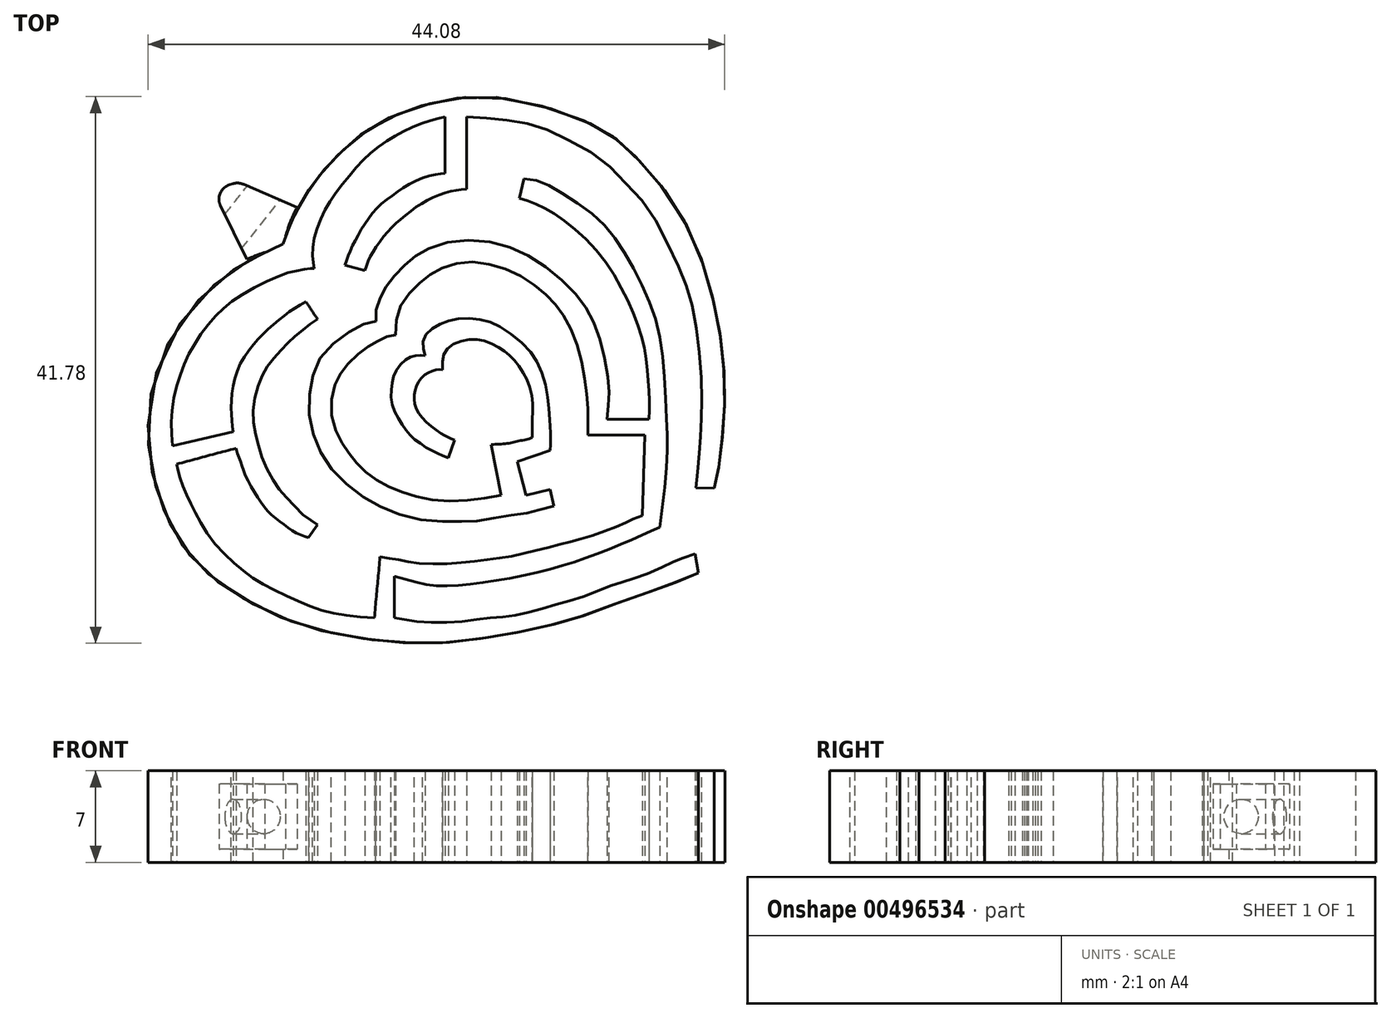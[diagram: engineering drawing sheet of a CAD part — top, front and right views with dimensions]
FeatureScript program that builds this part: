
annotation { "Feature Type Name" : "Feature", "Feature Type Description" : "" }
export const myFeature = defineFeature(function(context is Context, id is Id, definition is map)
    precondition{}
    {
        {
            var Q0;
            Q0=qCreatedBy(makeId("Top.planeOp"),FACE);
            var sketch = newSketch(context, id + "F0", { "sketchPlane" : qUnion([Q0])});
            skFitSpline(sketch, "E0", {"points": [v(62.05, 22.52) * mm, v(60.63, 22.56) * mm], "startDerivative": vector(-1.42, 0.04) * mm, "endDerivative": vector(-1.42, 0.04) * mm});
            skFitSpline(sketch, "E1", {"points": [v(60.63, 22.56) * mm, v(60.77, 23.68) * mm, v(60.9, 25.24) * mm, v(60.98, 26.5) * mm, v(61.06, 28.05) * mm, v(61.1, 29.64) * mm, v(60.96, 32.3) * mm, v(60.63, 35.06) * mm, v(60.14, 37.28) * mm, v(59.52, 38.95) * mm, v(58.29, 41.63) * mm, v(56.87, 44.04) * mm, v(55.17, 45.95) * mm, v(53.45, 47.62) * mm, v(50.93, 49.09) * mm, v(48.74, 50.12) * mm, v(46.91, 50.53) * mm, v(44.93, 50.79) * mm, v(43.1, 50.9) * mm], "startDerivative": vector(3.34, 25.94) * mm, "endDerivative": vector(-34.59, 1.48) * mm});
            skFitSpline(sketch, "E2", {"points": [v(43.1, 50.9) * mm, v(43.1, 45.38) * mm], "startDerivative": vector(0, -5.52) * mm, "endDerivative": vector(0, -5.52) * mm});
            skFitSpline(sketch, "E3", {"points": [v(43.1, 45.38) * mm, v(42.1, 45.24) * mm, v(40.77, 44.82) * mm, v(39.39, 44.09) * mm, v(38.14, 43.1) * mm, v(37.13, 42.18) * mm, v(36.24, 41.01) * mm, v(35.66, 40.02) * mm, v(35.32, 39.16) * mm], "startDerivative": vector(-9.38, -0.74) * mm, "endDerivative": vector(-3.58, -8.09) * mm});
            skFitSpline(sketch, "E4", {"points": [v(35.32, 39.16) * mm, v(33.83, 39.57) * mm], "startDerivative": vector(-1.5, 0.4) * mm, "endDerivative": vector(-1.5, 0.4) * mm});
            skFitSpline(sketch, "E5", {"points": [v(33.83, 39.57) * mm, v(34.06, 40.22) * mm, v(34.37, 41) * mm, v(34.85, 41.9) * mm, v(35.49, 42.93) * mm, v(36.25, 43.9) * mm, v(37.22, 44.73) * mm, v(38.3, 45.48) * mm, v(39.63, 46.2) * mm, v(40.85, 46.51) * mm, v(41.47, 46.59) * mm], "startDerivative": vector(2.94, 7.47) * mm, "endDerivative": vector(8.21, 1.68) * mm});
            skFitSpline(sketch, "E6", {"points": [v(41.47, 46.59) * mm, v(41.47, 50.9) * mm], "startDerivative": vector(0, 4.3) * mm, "endDerivative": vector(0, 4.3) * mm});
            skFitSpline(sketch, "E7", {"points": [v(41.47, 50.9) * mm, v(40.43, 50.66) * mm, v(38.77, 50.03) * mm, v(37.26, 49.2) * mm, v(35.71, 48.06) * mm, v(34.3, 46.59) * mm, v(32.94, 44.82) * mm, v(32, 43.2) * mm, v(31.42, 41.34) * mm, v(31.36, 40.04) * mm, v(31.46, 39.3) * mm], "startDerivative": vector(-11.85, -2.33) * mm, "endDerivative": vector(1.18, -8.66) * mm});
            skFitSpline(sketch, "E8", {"points": [v(31.46, 39.3) * mm, v(31.18, 39.3) * mm, v(30.33, 39.18) * mm, v(28.76, 38.73) * mm, v(25.7, 37.15) * mm, v(23.85, 35.6) * mm, v(22.25, 33.4) * mm, v(21.25, 31.22) * mm, v(20.6, 28.45) * mm, v(20.64, 25.75) * mm], "startDerivative": vector(-5.79, 0.27) * mm, "endDerivative": vector(1.44, -20.53) * mm});
            skFitSpline(sketch, "E9", {"points": [v(20.64, 25.75) * mm, v(25.29, 26.84) * mm], "startDerivative": vector(4.64, 1.09) * mm, "endDerivative": vector(4.64, 1.09) * mm});
            skFitSpline(sketch, "E10", {"points": [v(25.29, 26.84) * mm, v(25.17, 27.73) * mm, v(25.13, 28.97) * mm, v(25.29, 30.46) * mm, v(25.87, 32.1) * mm, v(26.84, 33.49) * mm, v(27.77, 34.5) * mm, v(28.87, 35.45) * mm, v(29.81, 36.17) * mm, v(30.82, 36.76) * mm], "startDerivative": vector(-1.46, 9.4) * mm, "endDerivative": vector(9.13, 5.8) * mm});
            skFitSpline(sketch, "E11", {"points": [v(30.82, 36.76) * mm, v(31.73, 35.45) * mm], "startDerivative": vector(1.07, -1.31) * mm, "endDerivative": vector(1.07, -1.31) * mm});
            skFitSpline(sketch, "E12", {"points": [v(31.73, 35.45) * mm, v(30.82, 34.79) * mm, v(29.81, 33.96) * mm, v(28.86, 32.97) * mm, v(27.9, 31.82) * mm, v(27.22, 30.44) * mm, v(26.79, 28.37) * mm, v(27.04, 26.48) * mm, v(27.58, 24.62) * mm, v(28.56, 22.77) * mm, v(29.62, 21.51) * mm, v(30.91, 20.24) * mm, v(31.73, 19.72) * mm], "startDerivative": vector(-15.63, -7.02) * mm, "endDerivative": vector(11.82, -10.7) * mm});
            skFitSpline(sketch, "E13", {"points": [v(31.73, 19.72) * mm, v(31.01, 18.74) * mm], "startDerivative": vector(-0.73, -1) * mm, "endDerivative": vector(-0.73, -1) * mm});
            skFitSpline(sketch, "E14", {"points": [v(31.01, 18.74) * mm, v(30.18, 19.05) * mm, v(29.18, 19.72) * mm, v(28.1, 20.56) * mm, v(27.22, 21.72) * mm, v(26.23, 23.43) * mm, v(25.85, 24.53) * mm, v(25.48, 25.56) * mm], "startDerivative": vector(-5.96, 2.5) * mm, "endDerivative": vector(-2.37, 9.5) * mm});
            skFitSpline(sketch, "E15", {"points": [v(25.48, 25.56) * mm, v(20.96, 24.36) * mm], "startDerivative": vector(-4.66, -1.2) * mm, "endDerivative": vector(-4.66, -1.2) * mm});
            skFitSpline(sketch, "E16", {"points": [v(20.96, 24.36) * mm, v(21.08, 23.82) * mm, v(21.4, 22.81) * mm, v(21.85, 21.7) * mm, v(22.55, 20.33) * mm, v(23.66, 18.54) * mm, v(25.48, 16.68) * mm, v(27.06, 15.47) * mm, v(29.1, 14.4) * mm, v(31.28, 13.46) * mm, v(33.37, 12.87) * mm, v(36.07, 12.6) * mm], "startDerivative": vector(1.94, -9.96) * mm, "endDerivative": vector(24.7, -2.32) * mm});
            skFitSpline(sketch, "E17", {"points": [v(36.07, 12.6) * mm, v(36.5, 17.27) * mm], "startDerivative": vector(0.43, 4.86) * mm, "endDerivative": vector(0.43, 4.86) * mm});
            skFitSpline(sketch, "E18", {"points": [v(36.5, 17.27) * mm, v(37.72, 17.09) * mm, v(39.05, 16.83) * mm, v(41.6, 16.75) * mm, v(44.13, 16.98) * mm, v(46.27, 17.27) * mm, v(48.3, 17.72) * mm, v(50.4, 18.25) * mm, v(51.96, 18.66) * mm, v(54.08, 19.39) * mm, v(55.48, 19.96) * mm, v(56.54, 20.43) * mm], "startDerivative": vector(16.41, -3.48) * mm, "endDerivative": vector(19.07, 6.04) * mm});
            skFitSpline(sketch, "E19", {"points": [v(56.54, 20.43) * mm, v(56.75, 26.58) * mm], "startDerivative": vector(0.21, 6.16) * mm, "endDerivative": vector(0.21, 6.16) * mm});
            skFitSpline(sketch, "E20", {"points": [v(56.75, 26.58) * mm, v(52.39, 26.58) * mm], "startDerivative": vector(-4.36, 0) * mm, "endDerivative": vector(-4.36, 0) * mm});
            skFitSpline(sketch, "E21", {"points": [v(52.39, 26.58) * mm, v(52.39, 28.3) * mm, v(52.22, 30.32) * mm, v(51.7, 33.05) * mm, v(50.65, 35.5) * mm, v(49.58, 36.9) * mm, v(47.89, 38.34) * mm, v(45.41, 39.49) * mm, v(42.83, 39.78) * mm, v(40.72, 39.09) * mm, v(39.35, 38.03) * mm, v(38, 36.34) * mm, v(37.68, 34.23) * mm], "startDerivative": vector(0.45, 23.14) * mm, "endDerivative": vector(-0.75, -26.8) * mm});
            skFitSpline(sketch, "E22", {"points": [v(37.68, 34.23) * mm, v(36.96, 34.07) * mm, v(36.08, 33.61) * mm, v(35.02, 32.93) * mm, v(33.77, 31.66) * mm, v(33.11, 30.57) * mm, v(32.77, 28.4) * mm, v(33.37, 26.38) * mm, v(34.17, 25.13) * mm, v(35.11, 24) * mm, v(36.42, 23.03) * mm, v(38.1, 22.26) * mm, v(40.25, 21.65) * mm, v(43.1, 21.57) * mm, v(45.75, 21.96) * mm], "startDerivative": vector(-15.15, -2.3) * mm, "endDerivative": vector(28.8, 5.22) * mm});
            skFitSpline(sketch, "E23", {"points": [v(45.75, 21.96) * mm, v(44.99, 25.85) * mm], "startDerivative": vector(-0.76, 3.9) * mm, "endDerivative": vector(-0.76, 3.9) * mm});
            skFitSpline(sketch, "E24", {"points": [v(44.99, 25.85) * mm, v(46.26, 25.94) * mm, v(47.23, 26.14) * mm, v(48.15, 26.4) * mm], "startDerivative": vector(3.6, 0.22) * mm, "endDerivative": vector(2.73, 1.23) * mm});
            skFitSpline(sketch, "E25", {"points": [v(48.15, 26.4) * mm, v(48.15, 28.1) * mm, v(48.15, 29.3) * mm, v(47.77, 30.71) * mm, v(47.15, 31.8) * mm, v(46.42, 32.65) * mm, v(45.75, 33.17) * mm, v(44.58, 33.73) * mm, v(43.45, 33.89) * mm, v(42.07, 33.5) * mm, v(41.38, 32.77) * mm, v(41.28, 31.58) * mm], "startDerivative": vector(-0.22, 11.54) * mm, "endDerivative": vector(0.38, -14.22) * mm});
            skFitSpline(sketch, "E26", {"points": [v(41.28, 31.58) * mm, v(40.85, 31.58) * mm, v(40.26, 31.39) * mm, v(39.65, 30.94) * mm, v(39.22, 30.14) * mm, v(39.1, 29.43) * mm, v(39.3, 28.54) * mm, v(40.04, 27.56) * mm, v(41.22, 26.68) * mm, v(41.73, 26.4) * mm, v(42.2, 26.2) * mm], "startDerivative": vector(-5.5, 0.39) * mm, "endDerivative": vector(4.74, -1.36) * mm});
            skFitSpline(sketch, "E27", {"points": [v(42.2, 26.2) * mm, v(41.73, 24.84) * mm], "startDerivative": vector(-0.46, -1.36) * mm, "endDerivative": vector(-0.46, -1.36) * mm});
            skFitSpline(sketch, "E28", {"points": [v(41.73, 24.84) * mm, v(40.84, 25.2) * mm, v(39.8, 25.78) * mm, v(38.81, 26.56) * mm, v(38.1, 27.5) * mm, v(37.44, 28.89) * mm, v(37.4, 30.34) * mm, v(37.74, 31.54) * mm, v(38.62, 32.45) * mm, v(39.33, 32.66) * mm, v(39.94, 32.63) * mm], "startDerivative": vector(-9.44, 3.5) * mm, "endDerivative": vector(5.62, -2.98) * mm});
            skFitSpline(sketch, "E29", {"points": [v(39.94, 32.63) * mm, v(39.8, 33.25) * mm, v(39.8, 33.82) * mm, v(40.17, 34.43) * mm, v(40.94, 34.96) * mm, v(41.87, 35.34) * mm, v(43.06, 35.49) * mm, v(44.46, 35.36) * mm, v(45.67, 34.87) * mm, v(47.41, 33.57) * mm, v(48.45, 32.26) * mm, v(49.1, 30.6) * mm, v(49.39, 28.9) * mm, v(49.5, 27.37) * mm, v(49.54, 25.71) * mm, v(49.5, 25.4) * mm], "startDerivative": vector(-3.21, 12.69) * mm, "endDerivative": vector(-1.92, -8.65) * mm});
            skFitSpline(sketch, "E30", {"points": [v(49.5, 25.4) * mm, v(47, 24.56) * mm], "startDerivative": vector(-2.5, -0.85) * mm, "endDerivative": vector(-2.5, -0.85) * mm});
            skFitSpline(sketch, "E31", {"points": [v(47, 24.56) * mm, v(47.65, 21.96) * mm], "startDerivative": vector(0.66, -2.6) * mm, "endDerivative": vector(0.66, -2.6) * mm});
            skFitSpline(sketch, "E32", {"points": [v(47.65, 21.96) * mm, v(49.5, 22.42) * mm], "startDerivative": vector(1.84, 0.46) * mm, "endDerivative": vector(1.84, 0.46) * mm});
            skFitSpline(sketch, "E33", {"points": [v(49.5, 22.42) * mm, v(49.8, 21.16) * mm], "startDerivative": vector(0.3, -1.26) * mm, "endDerivative": vector(0.3, -1.26) * mm});
            skFitSpline(sketch, "E34", {"points": [v(49.8, 21.16) * mm, v(48.5, 20.8) * mm, v(47.48, 20.56) * mm, v(45.75, 20.35) * mm, v(43.97, 20) * mm, v(42.52, 19.98) * mm, v(39.93, 20.06) * mm, v(37.16, 20.83) * mm, v(35.05, 21.96) * mm, v(33, 23.74) * mm, v(31.72, 25.74) * mm, v(31.1, 28.1) * mm, v(31.21, 30.47) * mm, v(31.93, 32.47) * mm, v(33.62, 34.13) * mm, v(35.24, 35.04) * mm, v(36.2, 35.3) * mm], "startDerivative": vector(-26.51, -7.02) * mm, "endDerivative": vector(23.37, 2.43) * mm});
            skFitSpline(sketch, "E35", {"points": [v(36.2, 35.3) * mm, v(36.2, 36.21) * mm, v(36.68, 37.4) * mm, v(37.37, 38.48) * mm, v(38.55, 39.7) * mm, v(39.79, 40.61) * mm, v(42.52, 41.44) * mm, v(45.92, 41.08) * mm, v(48.77, 39.7) * mm, v(51.22, 37.61) * mm, v(52.55, 35.79) * mm, v(53.42, 33.47) * mm, v(53.93, 30.8) * mm, v(53.98, 29.2) * mm, v(53.84, 27.78) * mm], "startDerivative": vector(-1.9, 18.54) * mm, "endDerivative": vector(-3.11, -26.6) * mm});
            skFitSpline(sketch, "E36", {"points": [v(53.84, 27.78) * mm, v(57.07, 27.78) * mm], "startDerivative": vector(3.22, 0) * mm, "endDerivative": vector(3.22, 0) * mm});
            skFitSpline(sketch, "E37", {"points": [v(57.07, 27.78) * mm, v(57.07, 29.46) * mm, v(56.95, 31.42) * mm, v(56.56, 33.82) * mm, v(55.51, 36.65) * mm, v(53.44, 40.22) * mm, v(50.54, 42.98) * mm, v(48.57, 44.17) * mm, v(47.15, 44.69) * mm], "startDerivative": vector(0.5, 16.86) * mm, "endDerivative": vector(-15.63, 5) * mm});
            skFitSpline(sketch, "E38", {"points": [v(47.15, 44.69) * mm, v(47.5, 46.18) * mm], "startDerivative": vector(0.34, 1.5) * mm, "endDerivative": vector(0.34, 1.5) * mm});
            skFitSpline(sketch, "E39", {"points": [v(47.5, 46.18) * mm, v(48.8, 45.94) * mm, v(50.43, 45.04) * mm, v(52.7, 43.53) * mm, v(54.27, 41.86) * mm, v(55.7, 39.68) * mm, v(56.93, 37.11) * mm, v(57.81, 34.46) * mm, v(58.23, 31.22) * mm, v(58.4, 27.67) * mm, v(58.47, 25.64) * mm, v(58.29, 22.86) * mm, v(57.87, 19.53) * mm], "startDerivative": vector(21.84, -2.2) * mm, "endDerivative": vector(-4.8, -35.34) * mm});
            skFitSpline(sketch, "E40", {"points": [v(57.87, 19.53) * mm, v(55.96, 18.67) * mm, v(52.9, 17.42) * mm, v(49.86, 16.43) * mm, v(45.98, 15.55) * mm, v(42.5, 15.1) * mm, v(40.08, 15.14) * mm, v(37.6, 15.8) * mm], "startDerivative": vector(-14.97, -6.87) * mm, "endDerivative": vector(-19.58, 4.47) * mm});
            skFitSpline(sketch, "E41", {"points": [v(37.6, 15.8) * mm, v(37.6, 12.6) * mm], "startDerivative": vector(0, -3.02) * mm, "endDerivative": vector(0, -3.02) * mm});
            skFitSpline(sketch, "E42", {"points": [v(37.6, 12.6) * mm, v(39.24, 12.34) * mm, v(42.2, 12.28) * mm, v(44.89, 12.6) * mm, v(46.93, 12.8) * mm, v(49.43, 13.48) * mm, v(52, 14.21) * mm, v(54.49, 15.18) * mm, v(56.45, 15.8) * mm, v(58.97, 16.9) * mm, v(60.59, 17.5) * mm], "startDerivative": vector(16.14, -2.23) * mm, "endDerivative": vector(28.15, 10.55) * mm});
            skFitSpline(sketch, "E43", {"points": [v(60.59, 17.5) * mm, v(60.85, 16.05) * mm], "startDerivative": vector(0.26, -1.45) * mm, "endDerivative": vector(0.26, -1.45) * mm});
            skFitSpline(sketch, "E44", {"points": [v(60.85, 16.05) * mm, v(59.54, 15.5) * mm, v(57.8, 14.84) * mm, v(55.84, 14.17) * mm, v(52.68, 13) * mm, v(50.9, 12.42) * mm, v(48.05, 11.7) * mm, v(45.25, 11.19) * mm, v(42.16, 10.77) * mm, v(38.62, 10.7) * mm, v(35.05, 11.05) * mm, v(30.91, 11.92) * mm, v(27.2, 13.46) * mm, v(23.74, 15.66) * mm, v(21.45, 18.1) * mm, v(19.81, 21.29) * mm, v(18.87, 25.1) * mm, v(19.3, 31.04) * mm, v(22.55, 36.82) * mm, v(26.25, 39.8) * mm, v(29.07, 41.2) * mm], "startDerivative": vector(-38.93, -16.82) * mm, "endDerivative": vector(76.53, 36.47) * mm});
            skFitSpline(sketch, "E45", {"points": [v(29.07, 41.2) * mm, v(29.89, 43.25) * mm, v(31.37, 45.74) * mm, v(33.07, 47.76) * mm, v(35.98, 50.17) * mm, v(40.12, 51.86) * mm, v(45.56, 52.38) * mm, v(52.73, 50.3) * mm, v(55.63, 48.25) * mm, v(59.32, 43.7) * mm, v(61.76, 37.77) * mm, v(62.7, 32.65) * mm, v(62.8, 28.1) * mm, v(62.41, 24.33) * mm, v(62.05, 22.52) * mm], "startDerivative": vector(13.48, 38.17) * mm, "endDerivative": vector(-11.77, -25.16) * mm});
            skSolve(sketch);
        }
        {
            var Q0;
            Q0 = qSketchRegion(id + "F0", true);
            extrude(context, id + "F1", {"entities" : qUnion([Q0]), "depth" : 7 * mm, "offsetDistance" : 25 * mm, "symmetric" : true});
        }
        {
            var Q0;
            Q0=qCreatedBy(makeId("Top.planeOp"),FACE);
            var sketch = newSketch(context, id + "F2", { "sketchPlane" : qUnion([Q0])});
            skFitSpline(sketch, "E46.0.0", {"points": [v(62.05, 22.52) * mm, v(62.24, 22.92) * mm, v(62.42, 24.5) * mm, v(62.93, 28.2) * mm, v(62.8, 32.73) * mm, v(61.91, 37.87) * mm, v(59.72, 43.8) * mm, v(55.68, 48.4) * mm, v(52.92, 50.53) * mm, v(45.49, 52.93) * mm, v(40.2, 52.04) * mm, v(35.92, 50.45) * mm, v(33.04, 47.82) * mm, v(31.34, 45.83) * mm, v(29.81, 43.29) * mm, v(29.3, 41.86) * mm, v(29.07, 41.2) * mm]});
            skFitSpline(sketch, "E46.0.1", {"points": [v(29.07, 41.2) * mm, v(27.85, 40.6) * mm, v(26.28, 39.98) * mm, v(22.13, 36.98) * mm, v(18.78, 31.25) * mm, v(18.63, 25.13) * mm, v(19.67, 21.32) * mm, v(21.32, 17.98) * mm, v(23.64, 15.52) * mm, v(27.2, 13.35) * mm, v(30.83, 11.79) * mm, v(35.04, 11) * mm, v(38.58, 10.62) * mm, v(42.15, 10.7) * mm, v(45.26, 11.17) * mm, v(47.98, 11.66) * mm, v(50.96, 12.4) * mm, v(52.63, 12.96) * mm, v(55.87, 14.2) * mm, v(57.73, 14.8) * mm, v(59.53, 15.49) * mm, v(60.43, 15.87) * mm, v(60.85, 16.05) * mm]});
            skLineSegment(sketch, "E46.0.2", {"start": v(26.38, 39.88) * mm, "end": v(24.18, 44.37) * mm});
            skLineSegment(sketch, "E46.0.3", {"start": v(24.18, 44.37) * mm, "end": v(24.18, 45.46) * mm});
            skLineSegment(sketch, "E46.0.4", {"start": v(24.18, 45.46) * mm, "end": v(25.65, 45.92) * mm});
            skLineSegment(sketch, "E46.0.5", {"start": v(25.65, 45.92) * mm, "end": v(30.25, 43.95) * mm});
            skSolve(sketch);
        }
        {
            var Q0;
            Q0=makeQuery(id+"F2.imprint","IMPRINT",FACE,{"disambiguationData":[TD([[makeQuery(id+"F2.imprint","IMPRINT",EDGE,{"derivedFrom":sQuery(id+"F2.wireOp",EDGE,"E46.0.0")}),-1.0]])]});
            extrude(context, id + "F3", {"entities" : qUnion([Q0]), "operationType" : NewBodyOperationType.ADD, "depth" : 5 * mm, "offsetDistance" : 25 * mm, "symmetric" : true});
        }
        {
            var Q0;
            Q0=makeQuery(id+"F3.opExtrude","SWEPT_EDGE",EDGE,{"disambiguationData":[OSD([sQuery(id+"F2.wireOp",EDGE,"E46.0.3"),sQuery(id+"F2.wireOp",EDGE,"E46.0.4")])]});
            var Q1;
            Q1=makeQuery(id+"F3.opExtrude","SWEPT_EDGE",EDGE,{"disambiguationData":[OSD([sQuery(id+"F2.wireOp",EDGE,"E46.0.4"),sQuery(id+"F2.wireOp",EDGE,"E46.0.5")])]});
            var Q2;
            Q2=makeQuery(id+"F3.opExtrude","SWEPT_EDGE",EDGE,{"disambiguationData":[OSD([sQuery(id+"F2.wireOp",EDGE,"E46.0.2"),sQuery(id+"F2.wireOp",EDGE,"E46.0.3")])]});
            fillet(context, id + "F4", {"entities" : qUnion([Q0, Q1, Q2]), "radius" : 1.2 * mm, "tangentPropagation" : true, "allowEdgeOverflow" : false});
        }
        {
            var Q0;
            Q0=makeQuery(id+"F1.opExtrude","CAP_VERTEX",VERTEX,{"disambiguationData":[OSD([sQuery(id+"F0.wireOp",EDGE,"E44"),sQuery(id+"F0.wireOp",EDGE,"E45")])],"isStart":true});
            var Q1;
            Q1=makeQuery(id+"F1.opExtrude","CAP_VERTEX",VERTEX,{"disambiguationData":[OSD([sQuery(id+"F0.wireOp",EDGE,"E7"),sQuery(id+"F0.wireOp",EDGE,"E8")])],"isStart":true});
            var Q2;
            Q2=makeQuery(id+"F1.opExtrude","CAP_VERTEX",VERTEX,{"disambiguationData":[OSD([sQuery(id+"F0.wireOp",EDGE,"E44"),sQuery(id+"F0.wireOp",EDGE,"E45")])],"isStart":false});
            cPlane(context, id + "F5", {"entities" : qUnion([Q0, Q1, Q2]), "cplaneType" : CPlaneType.THREE_POINT, "offset" : 25 * mm, "width" : 150 * mm, "height" : 150 * mm});
        }
        {
            var Q0;
            Q0=qCreatedBy(id+"F5.planeOp",FACE);
            var sketch = newSketch(context, id + "F6", { "sketchPlane" : qUnion([Q0])});
            skCircle(sketch, "E47", {"center": v(6.42, 0) * mm, "radius": 1.32 * mm});
            skSolve(sketch);
        }
        {
            var Q0;
            Q0 = qSketchRegion(id + "F6", true);
            extrude(context, id + "F7", {"entities" : qUnion([Q0]), "operationType" : NewBodyOperationType.REMOVE, "oppositeDirection" : true, "depth" : 10 * mm, "offsetDistance" : 25 * mm, "symmetric" : true});
        }
    });
